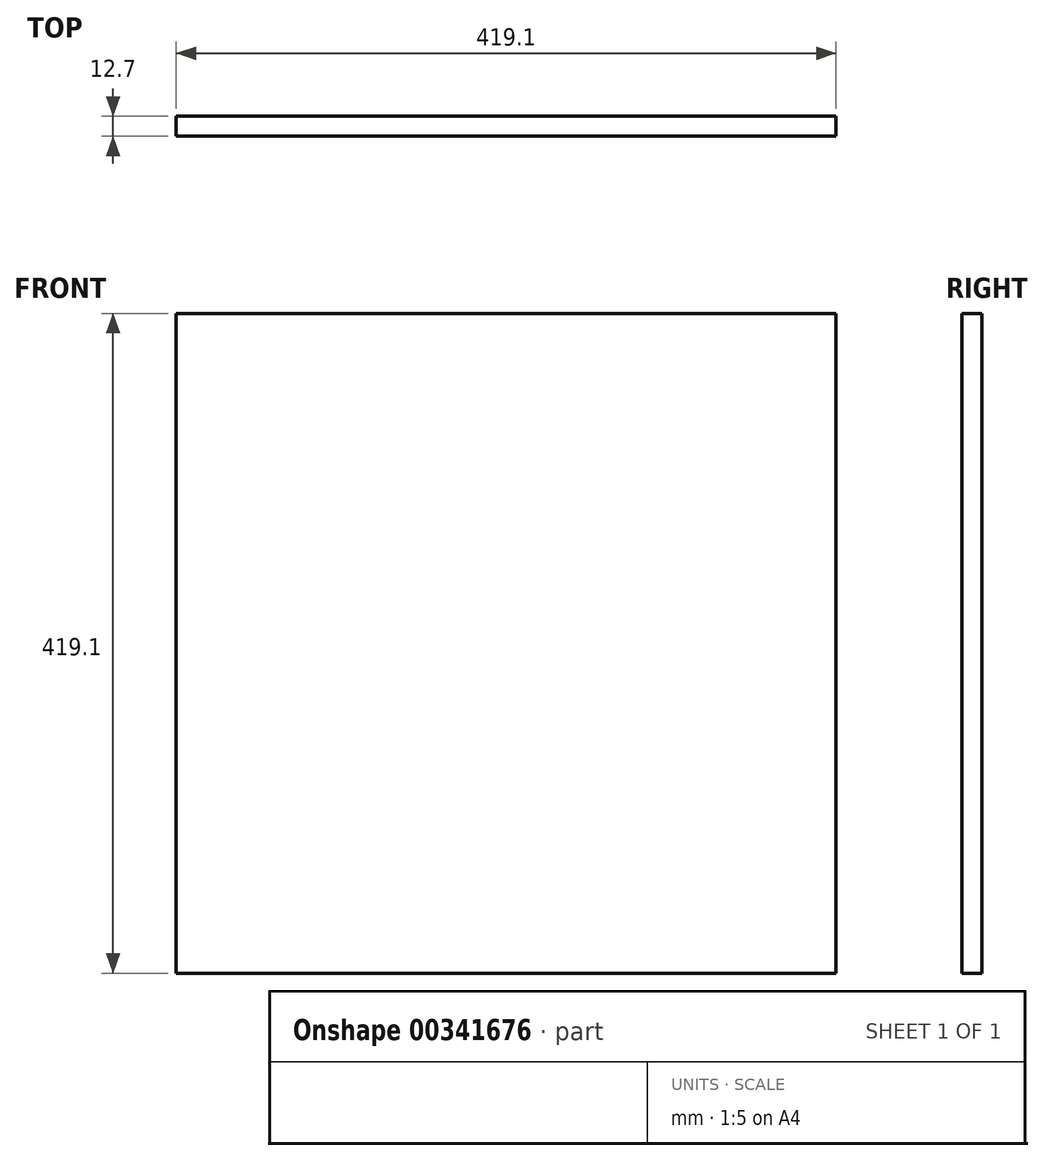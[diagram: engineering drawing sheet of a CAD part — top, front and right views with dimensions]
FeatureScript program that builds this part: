
annotation { "Feature Type Name" : "Feature", "Feature Type Description" : "" }
export const myFeature = defineFeature(function(context is Context, id is Id, definition is map)
    precondition{}
    {
        {
            var Q0;
            Q0=qCreatedBy(makeId("Front.planeOp"),FACE);
            var sketch = newSketch(context, id + "F0", { "sketchPlane" : qUnion([Q0])});
            skLineSegment(sketch, "E0.bottom", {"start": v(-204.08, 227.9) * mm, "end": v(215.02, 227.9) * mm});
            skLineSegment(sketch, "E0.top", {"start": v(-204.08, -191.2) * mm, "end": v(215.02, -191.2) * mm});
            skLineSegment(sketch, "E0.left", {"start": v(-204.08, 227.9) * mm, "end": v(-204.08, -191.2) * mm});
            skLineSegment(sketch, "E0.right", {"start": v(215.02, 227.9) * mm, "end": v(215.02, -191.2) * mm});
            skSolve(sketch);
        }
        {
            var Q0;
            Q0=makeQuery(id+"F0.imprint","IMPRINT",FACE,{"disambiguationData":[TD([[makeQuery(id+"F0.imprint","IMPRINT",EDGE,{"derivedFrom":sQuery(id+"F0.wireOp",EDGE,"E0.bottom")}),-1.0]])]});
            extrude(context, id + "F1", {"entities" : qUnion([Q0]), "depth" : 12.7 * mm, "offsetDistance" : 25.4 * mm});
        }
    });
